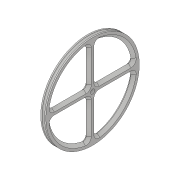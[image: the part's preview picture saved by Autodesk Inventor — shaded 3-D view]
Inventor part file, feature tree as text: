
AUTODESK INVENTOR PART (.ipt)
format: ipt  version: 2017 (Build 210142000, 142)  size: 198,656 bytes
history: native  units: in
note: dims shown in document units (in); Inventor stores cm internally (conversion verified against a paired STEP export)
features: sketch x3, extrude x2, revolve x1, fillet x1, chamfer x1
ambient origin geometry x8: Origin, YZ Plane, XZ Plane, XY Plane, X Axis, Y Axis, Z Axis, Center Point
bodies: Solid1 (feature_tree)
feature tree (8):
  revolve  "Revolution1"  [1 undecoded]
  extrude  "Extrusion1"  TaperAngle=90.0deg  [1 undecoded]
  fillet  "Fillet1"  Radius=4.0in
  extrude  "Extrusion2"  Depth=0.125in TaperAngle=0.0deg
  chamfer  "Chamfer1"  Distance=0.125in
  sketch  "Sketch1"  dims[d0=0.25in d1=2.25in]
  sketch  "Sketch2"  dims[d2=0.125in d3=90.0deg d4=4.0in]
  sketch  "Sketch3"  dims[d5=0.1875in d6=0.1875in d7=0.1875in d8=0.1875in d9=1.0in d10=0.0in d11=0.125in d12=0.2in d13=1.0in d14=0.0in d15=0.125in d16=0.125in d17=45.0deg]
note: 2 required parameter values undecoded (feature->parameter linkage not recoverable at this tier; creation-order binding heuristic only, values carry confidence <= 0.55)